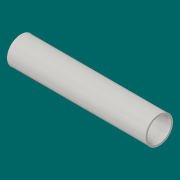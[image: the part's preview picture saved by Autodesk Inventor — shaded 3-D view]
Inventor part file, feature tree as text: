
AUTODESK INVENTOR PART (.ipt)
format: ipt  version: 2016 (Build 200138000, 138)  size: 76,800 bytes
history: native  units: mm
features: extrude x1, sketch x1
ambient origin geometry x8: Origin, YZ Plane, XZ Plane, XY Plane, X Axis, Y Axis, Z Axis, Center Point
bodies: Solid1 (feature_tree)
feature tree (2):
  extrude  "Extrusion1"  Depth=304.8mm
  sketch  "Sketch1"  dims[d0=60.325mm d1=51.9938mm d2=304.8mm d3=0.0mm]
